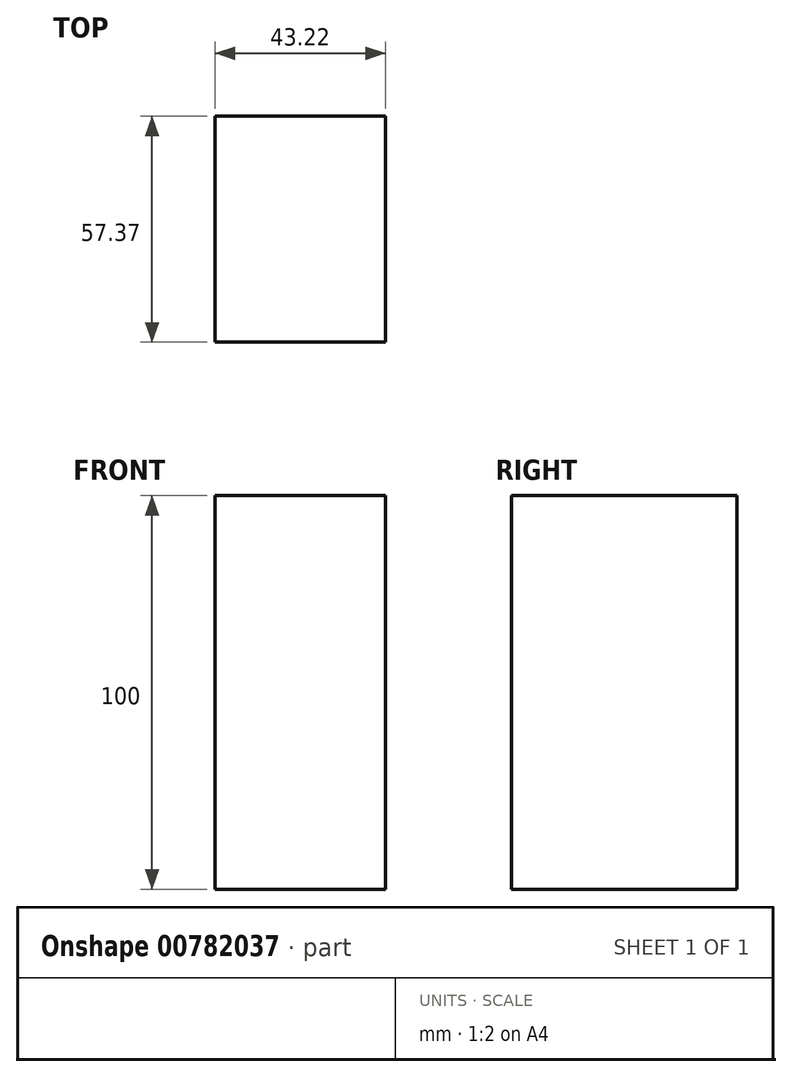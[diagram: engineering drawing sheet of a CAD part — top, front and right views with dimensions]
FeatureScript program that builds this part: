
annotation { "Feature Type Name" : "Feature", "Feature Type Description" : "" }
export const myFeature = defineFeature(function(context is Context, id is Id, definition is map)
    precondition{}
    {
        {
            var Q0;
            Q0=qCreatedBy(makeId("Top.planeOp"),FACE);
            var sketch = newSketch(context, id + "F0", { "sketchPlane" : qUnion([Q0])});
            skLineSegment(sketch, "E0.bottom", {"start": v(-168.75, -17.87) * mm, "end": v(17.69, -17.87) * mm});
            skLineSegment(sketch, "E0.top", {"start": v(-168.75, 39.5) * mm, "end": v(17.69, 39.5) * mm});
            skLineSegment(sketch, "E0.left", {"start": v(-168.75, -17.87) * mm, "end": v(-168.75, 39.5) * mm});
            skLineSegment(sketch, "E0.right", {"start": v(17.69, -17.87) * mm, "end": v(17.69, 39.5) * mm});
            skPoint(sketch, "E0.middle", {"position": v(-75.53, 10.82) * mm});
            skLineSegment(sketch, "E1.bottom", {"start": v(-75.53, 72.33) * mm, "end": v(-66.01, 72.33) * mm});
            skLineSegment(sketch, "E1.top", {"start": v(-75.53, 45.69) * mm, "end": v(-66.01, 45.69) * mm});
            skLineSegment(sketch, "E1.left", {"start": v(-75.53, 72.33) * mm, "end": v(-75.53, 45.69) * mm});
            skLineSegment(sketch, "E1.right", {"start": v(-66.01, 72.33) * mm, "end": v(-66.01, 45.69) * mm});
            skPoint(sketch, "E1.middle", {"position": v(-70.77, 59) * mm});
            skPoint(sketch, "E1.cornerSnap0", {"position": v(-75.53, 39.5) * mm});
            skLineSegment(sketch, "E2.bottom", {"start": v(-125.53, 39.5) * mm, "end": v(-25.53, 39.5) * mm});
            skLineSegment(sketch, "E2.top", {"start": v(-125.53, -17.87) * mm, "end": v(-25.53, -17.87) * mm});
            skLineSegment(sketch, "E2.left", {"start": v(-125.53, 39.5) * mm, "end": v(-125.53, -17.87) * mm});
            skLineSegment(sketch, "E2.right", {"start": v(-25.53, 39.5) * mm, "end": v(-25.53, -17.87) * mm});
            skLineSegment(sketch, "E3.bottom", {"start": v(-116.26, 39.5) * mm, "end": v(-16.26, 39.5) * mm});
            skLineSegment(sketch, "E3.top", {"start": v(-116.26, 39.5) * mm, "end": v(-16.26, 39.5) * mm});
            skLineSegment(sketch, "E3.left", {"start": v(-116.26, 39.5) * mm, "end": v(-116.26, 39.5) * mm});
            skLineSegment(sketch, "E3.right", {"start": v(-16.26, 39.5) * mm, "end": v(-16.26, 39.5) * mm});
            skPoint(sketch, "E3.middle", {"position": v(-66.26, 39.5) * mm});
            skSolve(sketch);
        }
        {
            var Q0;
            {var subQ0=sQuery(id+"F0.wireOp",EDGE,"E0.right");Q0=makeQuery(id+"F0.imprint","IMPRINT",FACE,{"disambiguationData":[TD([[makeQuery(id+"F0.imprint","IMPRINT",EDGE,{"derivedFrom":subQ0}),1.0]])]});}
            extrude(context, id + "F1", {"entities" : qUnion([Q0]), "depth" : 100 * mm, "offsetDistance" : 25 * mm});
        }
    });
